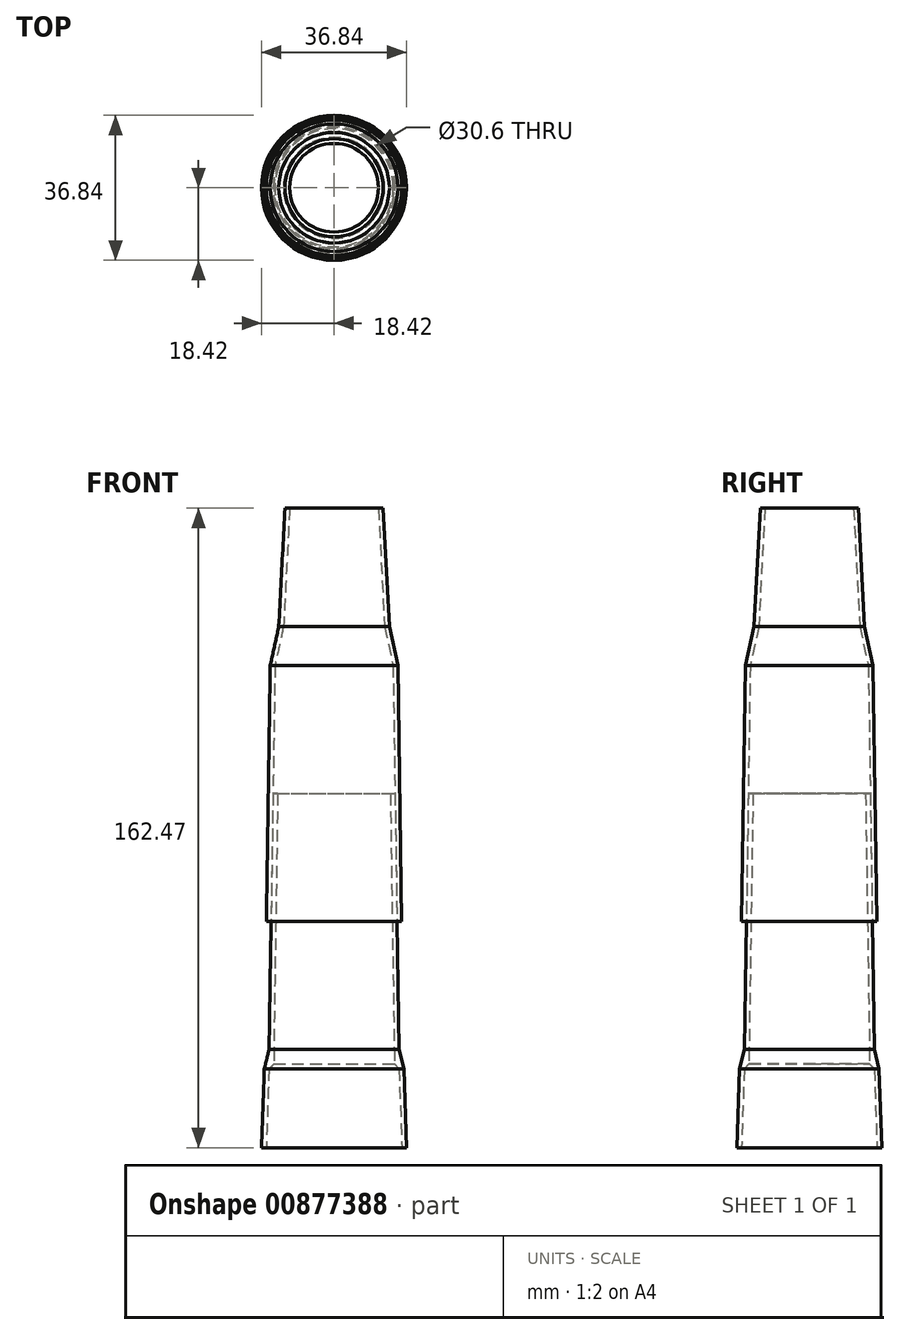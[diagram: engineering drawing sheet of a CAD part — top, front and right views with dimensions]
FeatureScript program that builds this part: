
annotation { "Feature Type Name" : "Feature", "Feature Type Description" : "" }
export const myFeature = defineFeature(function(context is Context, id is Id, definition is map)
    precondition{}
    {
        {
            var Q0;
            Q0=qCreatedBy(makeId("Front.planeOp"),FACE);
            var sketch = newSketch(context, id + "F0", { "sketchPlane" : qUnion([Q0])});
            skLineSegment(sketch, "E0", {"start": v(0, 0) * mm, "end": v(0, 90) * mm, "construction": true});
            skLineSegment(sketch, "E1", {"start": v(-15.5, 90) * mm, "end": v(-16.5, 25) * mm});
            skLineSegment(sketch, "E2", {"start": v(-15.5, 90) * mm, "end": v(-14.3, 89.97) * mm});
            skLineSegment(sketch, "E3", {"start": v(-14.3, 89.97) * mm, "end": v(-15.3, 25) * mm});
            skLineSegment(sketch, "E4", {"start": v(-18.42, 0) * mm, "end": v(-17.73, 20) * mm});
            skLineSegment(sketch, "E5", {"start": v(-17.73, 20) * mm, "end": v(-16.5, 25) * mm});
            skLineSegment(sketch, "E6", {"start": v(-18.42, 0) * mm, "end": v(-17.22, 0) * mm});
            skLineSegment(sketch, "E7", {"start": v(-17.22, 0) * mm, "end": v(-16.53, 20) * mm});
            skLineSegment(sketch, "E8", {"start": v(-16.53, 20) * mm, "end": v(-15.3, 21.23) * mm});
            skLineSegment(sketch, "E9", {"start": v(-15.3, 21.23) * mm, "end": v(-15.3, 25) * mm});
            skPoint(sketch, "E10", {"position": v(-16.88, 10) * mm});
            skPoint(sketch, "E11", {"position": v(-16, 57.5) * mm});
            skSolve(sketch);
        }
        {
            var Q0;
            Q0=qCreatedBy(makeId("Front.planeOp"),FACE);
            var sketch = newSketch(context, id + "F1", { "sketchPlane" : qUnion([Q0])});
            skLineSegment(sketch, "E12", {"start": v(0, 57.5) * mm, "end": v(0, 114.82) * mm, "construction": true});
            skLineSegment(sketch, "E13", {"start": v(-16, 57.5) * mm, "end": v(-15, 122.47) * mm});
            skLineSegment(sketch, "E14", {"start": v(-16, 57.5) * mm, "end": v(-17.2, 57.5) * mm});
            skLineSegment(sketch, "E15", {"start": v(-17.2, 57.5) * mm, "end": v(-16.2, 122.47) * mm});
            skLineSegment(sketch, "E16", {"start": v(-11.26, 162.47) * mm, "end": v(-12.84, 132.47) * mm});
            skLineSegment(sketch, "E17", {"start": v(-11.26, 162.47) * mm, "end": v(-12.46, 162.47) * mm});
            skLineSegment(sketch, "E18", {"start": v(-12.46, 162.47) * mm, "end": v(-14.04, 132.47) * mm});
            skPoint(sketch, "E19", {"position": v(-13.25, 147.47) * mm});
            skLineSegment(sketch, "E20", {"start": v(-14.04, 132.47) * mm, "end": v(-16.2, 122.47) * mm});
            skLineSegment(sketch, "E21", {"start": v(-12.84, 132.47) * mm, "end": v(-15, 122.47) * mm});
            skSolve(sketch);
        }
        {
            var Q0;
            Q0=makeQuery(id+"F0.imprint","IMPRINT",FACE,{"disambiguationData":[TD([[makeQuery(id+"F0.imprint","IMPRINT",EDGE,{"derivedFrom":sQuery(id+"F0.wireOp",EDGE,"E1")}),1.0]])]});
            var Q1;
            Q1=sQuery(id+"F0.wireOp",EDGE,"E0");
            revolve(context, id + "F2", {"surfaceOperationType" : NewSurfaceOperationType.NEW, "entities" : qUnion([Q0]), "axis" : qUnion([Q1]), "revolveType" : RevolveType.FULL});
        }
        {
            var Q0;
            Q0=makeQuery(id+"F1.imprint","IMPRINT",FACE,{"disambiguationData":[TD([[makeQuery(id+"F1.imprint","IMPRINT",EDGE,{"derivedFrom":sQuery(id+"F1.wireOp",EDGE,"E13")}),1.0]])]});
            var Q1;
            Q1=sQuery(id+"F1.wireOp",EDGE,"E12");
            revolve(context, id + "F3", {"surfaceOperationType" : NewSurfaceOperationType.NEW, "entities" : qUnion([Q0]), "axis" : qUnion([Q1]), "revolveType" : RevolveType.FULL});
        }
    });
